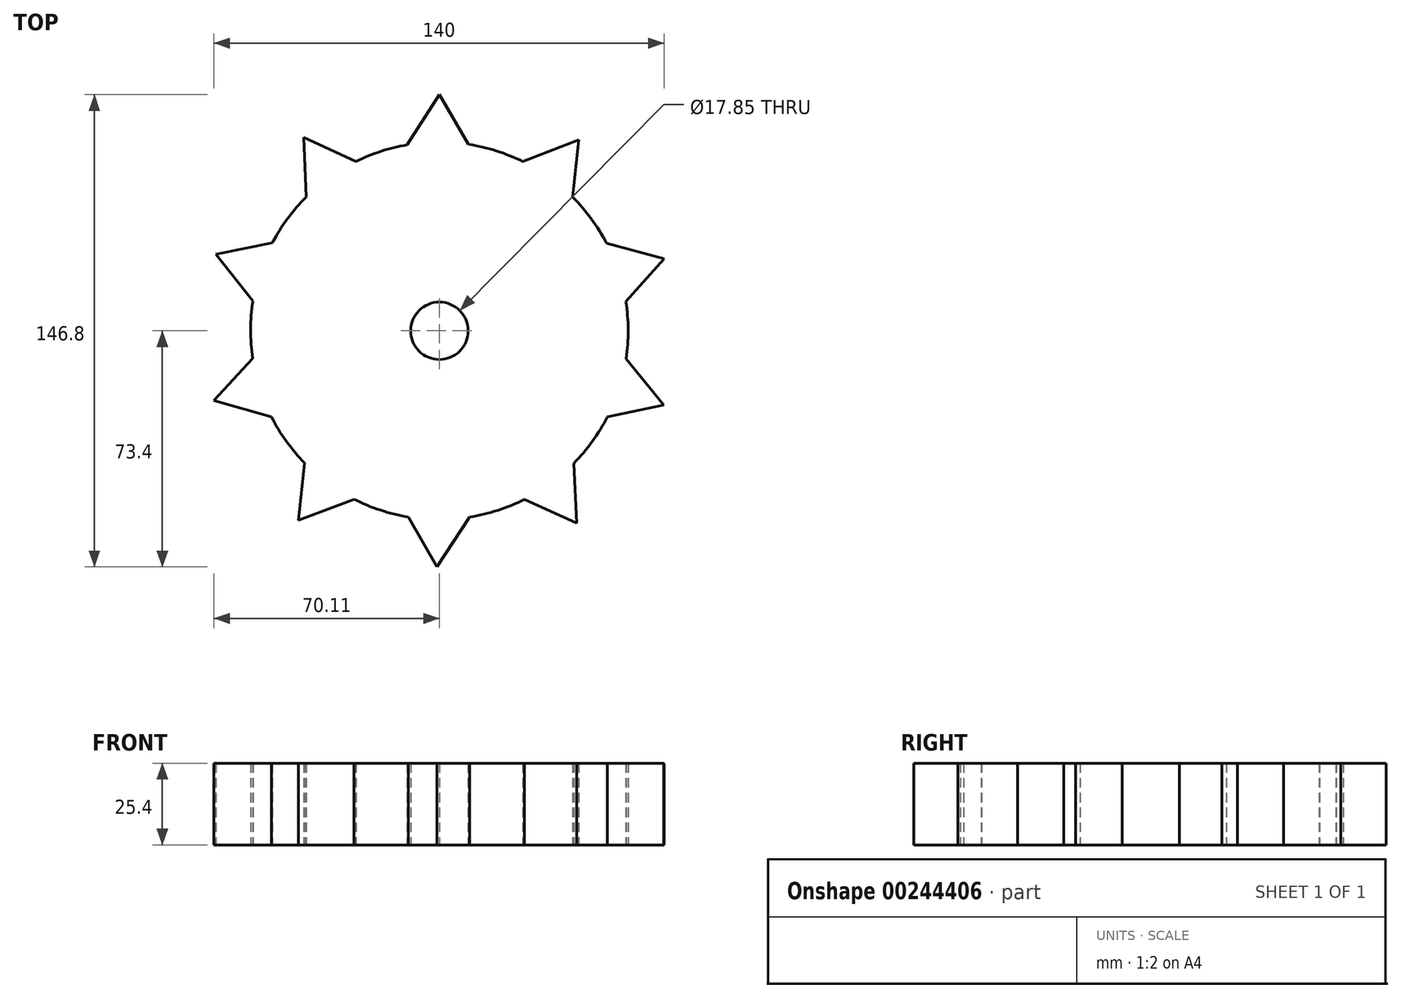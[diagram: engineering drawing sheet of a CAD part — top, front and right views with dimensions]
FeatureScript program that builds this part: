
annotation { "Feature Type Name" : "Feature", "Feature Type Description" : "" }
export const myFeature = defineFeature(function(context is Context, id is Id, definition is map)
    precondition{}
    {
        {
            var Q0;
            Q0=qCreatedBy(makeId("Top.planeOp"),FACE);
            var sketch = newSketch(context, id + "F0", { "sketchPlane" : qUnion([Q0])});
            skArc(sketch, "E0", {"start": v(-10.02, 57.81) * mm, "mid": v(-18.12, 55.8) * mm, "end": v(-25.86, 52.67) * mm});
            skLineSegment(sketch, "E1", {"start": v(0, 0) * mm, "end": v(0, 73.4) * mm, "construction": true});
            skLineSegment(sketch, "E2", {"start": v(0, 73.4) * mm, "end": v(-10.02, 57.81) * mm});
            skLineSegment(sketch, "E3", {"start": v(0, 73.4) * mm, "end": v(9.03, 57.97) * mm});
            skCircle(sketch, "E4", {"center": v(0, 0) * mm, "radius": 8.92 * mm});
            skLineSegment(sketch, "E5.1.0", {"start": v(43.26, 59.3) * mm, "end": v(25.97, 52.61) * mm});
            skLineSegment(sketch, "E5.1.1", {"start": v(43.26, 59.3) * mm, "end": v(41.46, 41.51) * mm});
            skLineSegment(sketch, "E5.2.0", {"start": v(69.9, 22.41) * mm, "end": v(51.99, 27.2) * mm});
            skLineSegment(sketch, "E5.2.1", {"start": v(69.9, 22.41) * mm, "end": v(57.96, 9.1) * mm});
            skLineSegment(sketch, "E5.3.0", {"start": v(69.67, -23.09) * mm, "end": v(58.03, -8.67) * mm});
            skLineSegment(sketch, "E5.3.1", {"start": v(69.67, -23.09) * mm, "end": v(52.2, -26.8) * mm});
            skLineSegment(sketch, "E5.4.0", {"start": v(42.68, -59.71) * mm, "end": v(41.77, -41.2) * mm});
            skLineSegment(sketch, "E5.4.1", {"start": v(42.68, -59.71) * mm, "end": v(26.36, -52.42) * mm});
            skLineSegment(sketch, "E5.5.0", {"start": v(-0.71, -73.4) * mm, "end": v(9.46, -57.9) * mm});
            skLineSegment(sketch, "E5.5.1", {"start": v(-0.71, -73.4) * mm, "end": v(-9.6, -57.88) * mm});
            skLineSegment(sketch, "E5.6.0", {"start": v(-43.83, -58.88) * mm, "end": v(-26.48, -52.36) * mm});
            skLineSegment(sketch, "E5.6.1", {"start": v(-43.83, -58.88) * mm, "end": v(-41.86, -41.1) * mm});
            skLineSegment(sketch, "E5.7.0", {"start": v(-70.1, -21.73) * mm, "end": v(-52.25, -26.7) * mm});
            skLineSegment(sketch, "E5.7.1", {"start": v(-70.1, -21.73) * mm, "end": v(-58.05, -8.54) * mm});
            skLineSegment(sketch, "E5.8.0", {"start": v(-69.45, 23.76) * mm, "end": v(-57.94, 9.23) * mm});
            skLineSegment(sketch, "E5.8.1", {"start": v(-69.45, 23.76) * mm, "end": v(-51.93, 27.31) * mm});
            skLineSegment(sketch, "E5.9.0", {"start": v(-42.1, 60.13) * mm, "end": v(-41.37, 41.6) * mm});
            skLineSegment(sketch, "E5.9.1", {"start": v(-42.1, 60.13) * mm, "end": v(-25.86, 52.67) * mm});
            skLineSegment(sketch, "E5.anchor1", {"start": v(0, 0) * mm, "end": v(-10.02, 57.81) * mm, "construction": true});
            skLineSegment(sketch, "E5.anchor2", {"start": v(0, 0) * mm, "end": v(-41.37, 41.6) * mm, "construction": true});
            skArc(sketch, "E6.trimOffspring", {"start": v(-41.37, 41.6) * mm, "mid": v(-47.2, 34.86) * mm, "end": v(-51.93, 27.31) * mm});
            skArc(sketch, "E7.trimOffspring", {"start": v(-57.94, 9.23) * mm, "mid": v(-58.67, 0.35) * mm, "end": v(-58.05, -8.54) * mm});
            skArc(sketch, "E8.trimOffspring", {"start": v(-52.25, -26.7) * mm, "mid": v(-47.6, -34.3) * mm, "end": v(-41.86, -41.1) * mm});
            skArc(sketch, "E9.trimOffspring", {"start": v(-26.48, -52.36) * mm, "mid": v(-18.25, -55.76) * mm, "end": v(-9.6, -57.88) * mm});
            skArc(sketch, "E10.trimOffspring", {"start": v(9.46, -57.9) * mm, "mid": v(18.12, -55.8) * mm, "end": v(26.36, -52.42) * mm});
            skArc(sketch, "E11.trimOffspring", {"start": v(41.77, -41.2) * mm, "mid": v(47.53, -34.4) * mm, "end": v(52.2, -26.8) * mm});
            skArc(sketch, "E12.trimOffspring", {"start": v(58.03, -8.67) * mm, "mid": v(58.67, 0.22) * mm, "end": v(57.96, 9.1) * mm});
            skArc(sketch, "E13.trimOffspring", {"start": v(51.99, 27.2) * mm, "mid": v(47.27, 34.76) * mm, "end": v(41.46, 41.51) * mm});
            skArc(sketch, "E14.trimOffspring", {"start": v(25.97, 52.61) * mm, "mid": v(17.7, 55.94) * mm, "end": v(9.03, 57.97) * mm});
            skSolve(sketch);
        }
        {
            var Q0;
            Q0 = qSketchRegion(id + "F0", true);
            extrude(context, id + "F1", {"entities" : qUnion([Q0]), "depth" : 25.4 * mm});
        }
    });
